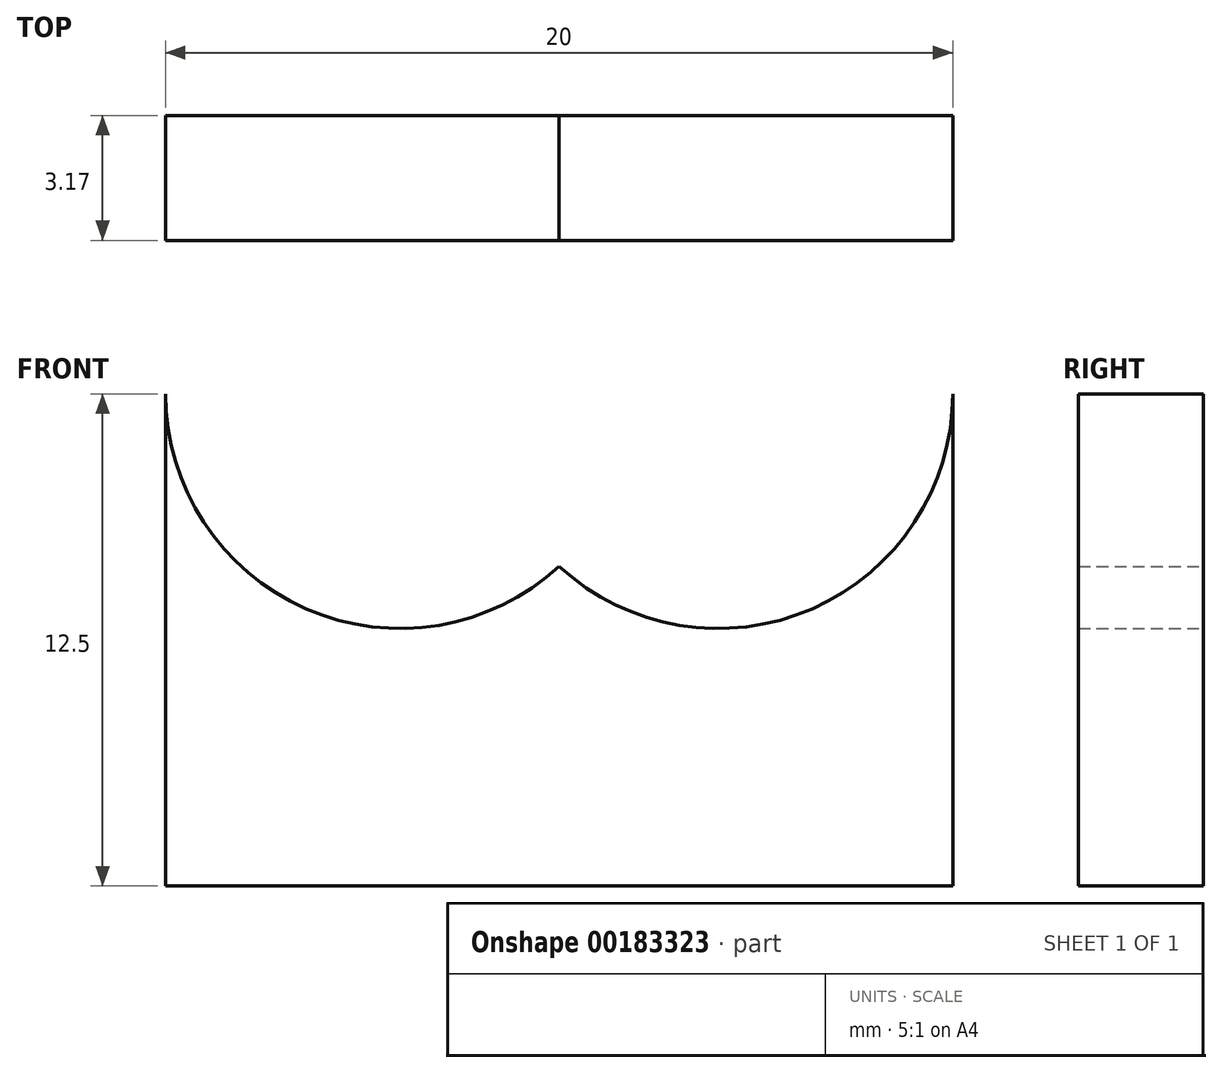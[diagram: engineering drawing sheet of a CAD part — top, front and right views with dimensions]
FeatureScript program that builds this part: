
annotation { "Feature Type Name" : "Feature", "Feature Type Description" : "" }
export const myFeature = defineFeature(function(context is Context, id is Id, definition is map)
    precondition{}
    {
        {
            var Q0;
            Q0=qCreatedBy(makeId("Front.planeOp"),FACE);
            var sketch = newSketch(context, id + "F0", { "sketchPlane" : qUnion([Q0])});
            skLineSegment(sketch, "E0", {"start": v(0, 0) * mm, "end": v(-10, 0) * mm});
            skLineSegment(sketch, "E1", {"start": v(-10, 0) * mm, "end": v(-10, 12.5) * mm});
            skLineSegment(sketch, "E2", {"start": v(0, 0) * mm, "end": v(0, 8.12) * mm});
            skArc(sketch, "E3", {"start": v(-10, 12.5) * mm, "mid": v(-6.43, 7.04) * mm, "end": v(0, 8.12) * mm});
            skArc(sketch, "E4.MirrorCS", {"start": v(10, 12.5) * mm, "mid": v(6.43, 7.04) * mm, "end": v(0, 8.12) * mm});
            skLineSegment(sketch, "E5.MirrorCS", {"start": v(0, 0) * mm, "end": v(10, 0) * mm});
            skLineSegment(sketch, "E6.MirrorCS", {"start": v(10, 0) * mm, "end": v(10, 12.5) * mm});
            skSolve(sketch);
        }
        {
            var Q0;
            Q0 = qSketchRegion(id + "F0", true);
            extrude(context, id + "F1", {"entities" : qUnion([Q0]), "depth" : 3.17 * mm});
        }
    });
